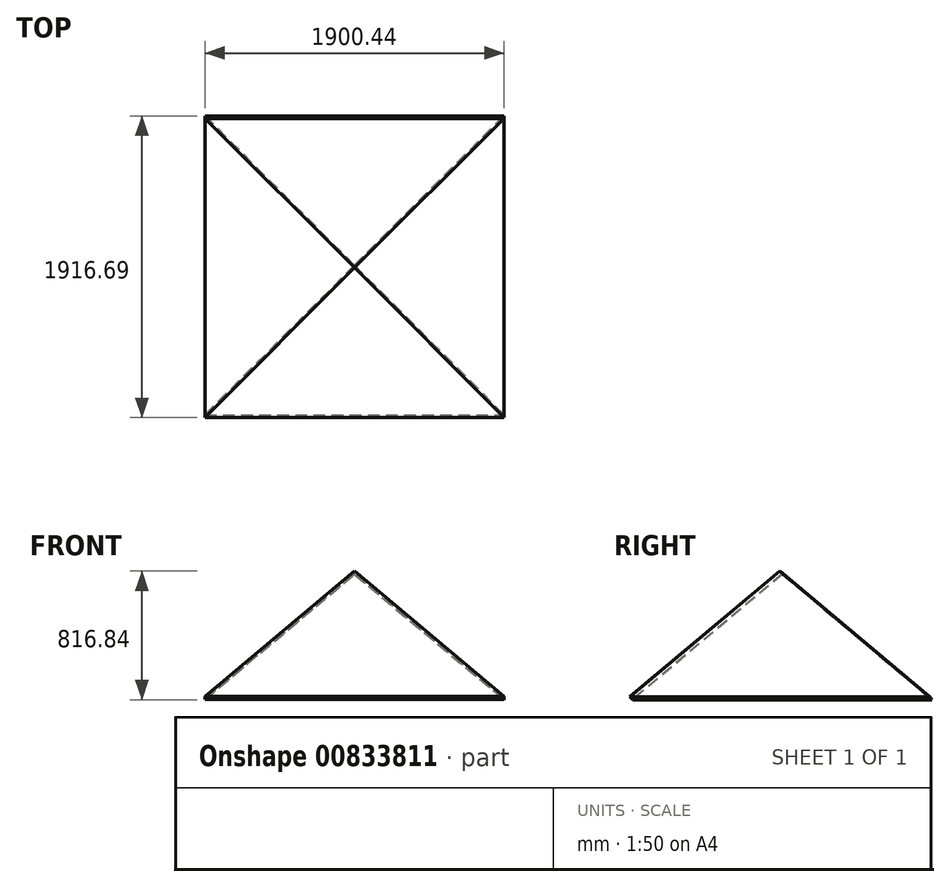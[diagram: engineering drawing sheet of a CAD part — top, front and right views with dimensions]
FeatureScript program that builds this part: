
annotation { "Feature Type Name" : "Feature", "Feature Type Description" : "" }
export const myFeature = defineFeature(function(context is Context, id is Id, definition is map)
    precondition{}
    {
        {
            var Q0;
            Q0=qCreatedBy(makeId("Top.planeOp"),FACE);
            var sketch = newSketch(context, id + "F0", { "sketchPlane" : qUnion([Q0])});
            skLineSegment(sketch, "E0", {"start": v(-650, -300) * mm, "end": v(300, -300) * mm});
            skLineSegment(sketch, "E1", {"start": v(300, -300) * mm, "end": v(300, 1600) * mm});
            skLineSegment(sketch, "E2", {"start": v(300, 1600) * mm, "end": v(-1600, 1600) * mm});
            skLineSegment(sketch, "E3", {"start": v(-1600, 1600) * mm, "end": v(-1600, -300) * mm});
            skLineSegment(sketch, "E4", {"start": v(-1600, -300) * mm, "end": v(-650, -300) * mm});
            skLineSegment(sketch, "E5", {"start": v(-650, -300) * mm, "end": v(-650, 1600) * mm});
            skLineSegment(sketch, "E6", {"start": v(-650, 1600) * mm, "end": v(-650, 650) * mm});
            skSolve(sketch);
        }
        {
            var Q0;
            Q0=sQuery(id+"F0.wireOp",EDGE,"E0");
            cPlane(context, id + "F1", {"entities" : qUnion([Q0]), "cplaneType" : CPlaneType.LINE_ANGLE, "offset" : 25 * mm, "angle" : 50 * degree, "oppositeDirection" : true, "width" : 150 * mm, "height" : 150 * mm});
        }
        {
            var Q0;
            Q0=qCreatedBy(id+"F1.planeOp",FACE);
            var sketch = newSketch(context, id + "F2", { "sketchPlane" : qUnion([Q0])});
            skLineSegment(sketch, "E7", {"start": v(-1599.67, 229.06) * mm, "end": v(300.77, 229.06) * mm});
            skLineSegment(sketch, "E8", {"start": v(300.77, 229.06) * mm, "end": v(-649.25, -1011.26) * mm});
            skLineSegment(sketch, "E9", {"start": v(-649.25, -1011.26) * mm, "end": v(-1599.67, 229.06) * mm});
            skSolve(sketch);
        }
        {
            var Q0;
            Q0=sQuery(id+"F0.wireOp",EDGE,"E5");
            cPoint(context, id + "F3", {"entities" : qUnion([Q0]), "parameter" : 0.5});
        }
        {
            var Q0;
            Q0 = qCreatedBy(id + "F3" ,VERTEX);
            var Q1;
            Q1=sQuery(id+"F0.wireOp",EDGE,"E5");
            cPlane(context, id + "F4", {"entities" : qUnion([Q0, Q1]), "cplaneType" : CPlaneType.LINE_POINT, "offset" : 25 * mm, "width" : 150 * mm, "height" : 150 * mm});
        }
        {
            var Q0;
            Q0=sQuery(id+"F0.wireOp",EDGE,"E1");
            cPlane(context, id + "F5", {"entities" : qUnion([Q0]), "cplaneType" : CPlaneType.LINE_ANGLE, "offset" : 25 * mm, "angle" : 40 * degree, "width" : 150 * mm, "height" : 150 * mm});
        }
        {
            var Q0;
            Q0=sQuery(id+"F0.wireOp",EDGE,"E2");
            cPlane(context, id + "F6", {"entities" : qUnion([Q0]), "cplaneType" : CPlaneType.LINE_ANGLE, "offset" : 25 * mm, "angle" : 50 * degree, "oppositeDirection" : true, "width" : 150 * mm, "height" : 150 * mm});
        }
        {
            var Q0;
            Q0=sQuery(id+"F0.wireOp",EDGE,"E3");
            cPlane(context, id + "F7", {"entities" : qUnion([Q0]), "cplaneType" : CPlaneType.LINE_ANGLE, "offset" : 25 * mm, "angle" : 40 * degree, "width" : 150 * mm, "height" : 150 * mm});
        }
        {
            var Q0;
            Q0=qCreatedBy(id+"F7.planeOp",FACE);
            var sketch = newSketch(context, id + "F8", { "sketchPlane" : qUnion([Q0])});
            skLineSegment(sketch, "E10", {"start": v(-1223.73, 300.95) * mm, "end": v(-1223.73, -1599.67) * mm});
            skLineSegment(sketch, "E11", {"start": v(-1223.73, -1599.67) * mm, "end": v(14.87, -650.87) * mm});
            skLineSegment(sketch, "E12", {"start": v(14.87, -650.87) * mm, "end": v(-1223.73, 300.95) * mm});
            skSolve(sketch);
        }
        {
            var Q0;
            Q0=qCreatedBy(id+"F6.planeOp",FACE);
            var sketch = newSketch(context, id + "F9", { "sketchPlane" : qUnion([Q0])});
            skLineSegment(sketch, "E13", {"start": v(300.34, -1224.41) * mm, "end": v(-1599.44, -1224.41) * mm});
            skLineSegment(sketch, "E14", {"start": v(-1599.44, -1224.41) * mm, "end": v(-649.58, 12.88) * mm});
            skLineSegment(sketch, "E15", {"start": v(-649.58, 12.88) * mm, "end": v(300.34, -1224.41) * mm});
            skSolve(sketch);
        }
        {
            var Q0;
            Q0=qCreatedBy(id+"F5.planeOp",FACE);
            var sketch = newSketch(context, id + "F10", { "sketchPlane" : qUnion([Q0])});
            skLineSegment(sketch, "E16", {"start": v(229.73, -299.85) * mm, "end": v(229.73, 1599.14) * mm});
            skLineSegment(sketch, "E17", {"start": v(229.73, 1599.14) * mm, "end": v(-1009.82, 651.31) * mm});
            skLineSegment(sketch, "E18", {"start": v(-1009.82, 651.31) * mm, "end": v(229.73, -299.85) * mm});
            skSolve(sketch);
        }
        {
            var Q0;
            Q0=makeQuery(id+"F2.imprint","IMPRINT",FACE,{"disambiguationData":[TD([[makeQuery(id+"F2.imprint","IMPRINT",EDGE,{"derivedFrom":sQuery(id+"F2.wireOp",EDGE,"E7")}),-1.0]])]});
            var Q1;
            Q1=makeQuery(id+"F8.imprint","IMPRINT",FACE,{"disambiguationData":[TD([[makeQuery(id+"F8.imprint","IMPRINT",EDGE,{"derivedFrom":sQuery(id+"F8.wireOp",EDGE,"E10")}),1.0]])]});
            var Q2;
            Q2=makeQuery(id+"F9.imprint","IMPRINT",FACE,{"disambiguationData":[TD([[makeQuery(id+"F9.imprint","IMPRINT",EDGE,{"derivedFrom":sQuery(id+"F9.wireOp",EDGE,"E13")}),-1.0]])]});
            var Q3;
            Q3=makeQuery(id+"F10.imprint","IMPRINT",FACE,{"disambiguationData":[TD([[makeQuery(id+"F10.imprint","IMPRINT",EDGE,{"derivedFrom":sQuery(id+"F10.wireOp",EDGE,"E16")}),1.0]])]});
            extrude(context, id + "F11", {"entities" : qUnion([Q0, Q1, Q2, Q3]), "depth" : 25 * mm, "offsetDistance" : 25 * mm});
        }
    });
